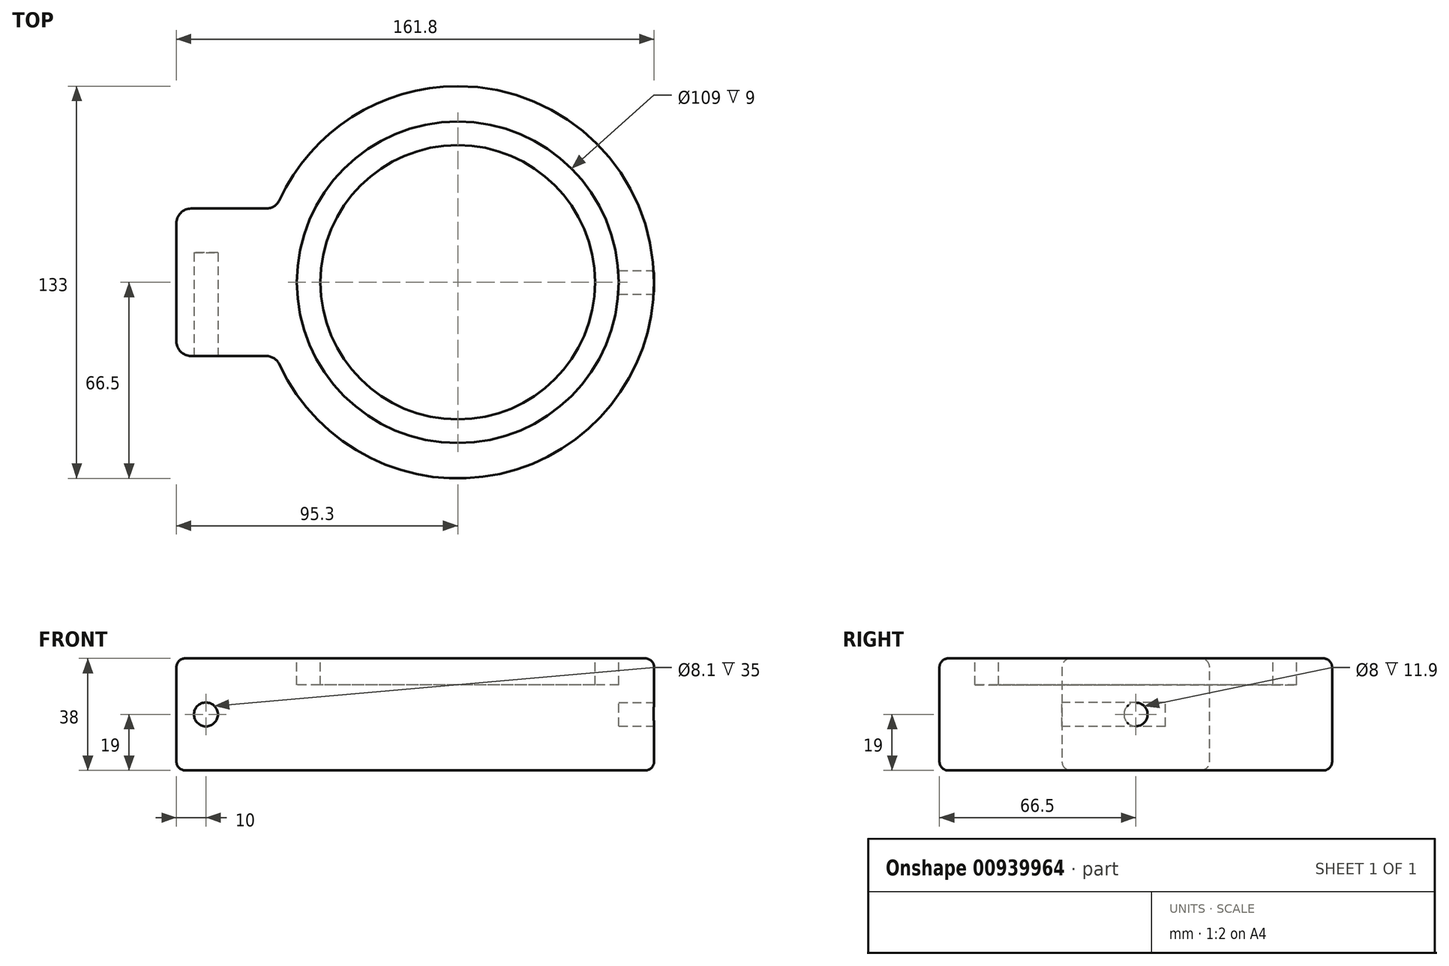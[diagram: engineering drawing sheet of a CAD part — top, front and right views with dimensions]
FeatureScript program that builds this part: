
annotation { "Feature Type Name" : "Feature", "Feature Type Description" : "" }
export const myFeature = defineFeature(function(context is Context, id is Id, definition is map)
    precondition{}
    {
        {
            var Q0;
            Q0=qCreatedBy(makeId("Top.planeOp"),FACE);
            var sketch = newSketch(context, id + "F0", { "sketchPlane" : qUnion([Q0])});
            skArc(sketch, "E0", {"start": v(-61.62, -25) * mm, "mid": v(66.5, 0) * mm, "end": v(-61.62, 25) * mm});
            skLineSegment(sketch, "E1", {"start": v(-61.62, 25) * mm, "end": v(-95.3, 25) * mm});
            skLineSegment(sketch, "E2", {"start": v(-95.3, 25) * mm, "end": v(-95.3, -25) * mm});
            skLineSegment(sketch, "E3", {"start": v(-95.3, -25) * mm, "end": v(-61.62, -25) * mm});
            skPoint(sketch, "E4.orphan", {"position": v(0, -25) * mm});
            skLineSegment(sketch, "E5", {"start": v(0, 66.5) * mm, "end": v(66.5, 66.5) * mm});
            skPoint(sketch, "E5.endSnap0", {"position": v(66.5, 0) * mm});
            skLineSegment(sketch, "E6", {"start": v(66.5, 66.5) * mm, "end": v(66.5, -67.23) * mm});
            skLineSegment(sketch, "E7", {"start": v(66.5, -67.23) * mm, "end": v(0, -66.5) * mm});
            skSolve(sketch);
        }
        {
            var Q0;
            Q0 = qSketchRegion(id + "F0", true);
            extrude(context, id + "F1", {"entities" : qUnion([Q0]), "depth" : 38 * mm, "offsetDistance" : 25 * mm});
        }
        {
            var Q0;
            Q0=makeQuery(id+"F1.opExtrude","SWEPT_EDGE",EDGE,{"disambiguationData":[OSD([sQuery(id+"F0.wireOp",EDGE,"E0"),sQuery(id+"F0.wireOp",EDGE,"E3")])]});
            var Q1;
            Q1=makeQuery(id+"F1.opExtrude","SWEPT_EDGE",EDGE,{"disambiguationData":[OSD([sQuery(id+"F0.wireOp",EDGE,"E0"),sQuery(id+"F0.wireOp",EDGE,"E1")])]});
            var Q2;
            Q2=makeQuery(id+"F1.opExtrude","SWEPT_EDGE",EDGE,{"disambiguationData":[OSD([sQuery(id+"F0.wireOp",EDGE,"E2"),sQuery(id+"F0.wireOp",EDGE,"E3")])]});
            var Q3;
            Q3=makeQuery(id+"F1.opExtrude","SWEPT_EDGE",EDGE,{"disambiguationData":[OSD([sQuery(id+"F0.wireOp",EDGE,"E1"),sQuery(id+"F0.wireOp",EDGE,"E2")])]});
            fillet(context, id + "F2", {"entities" : qUnion([Q0, Q1, Q2, Q3]), "radius" : 5 * mm, "tangentPropagation" : true, "allowEdgeOverflow" : false});
        }
        {
            var Q0;
            Q0=makeQuery(id+"F1.opExtrude","CAP_EDGE",EDGE,{"disambiguationData":[OSD([sQuery(id+"F0.wireOp",EDGE,"E2")])],"isStart":false});
            var Q1;
            Q1=makeQuery(id+"F1.opExtrude","CAP_EDGE",EDGE,{"disambiguationData":[OSD([sQuery(id+"F0.wireOp",EDGE,"E2")])],"isStart":true});
            fillet(context, id + "F3", {"entities" : qUnion([Q0, Q1]), "radius" : 3 * mm, "tangentPropagation" : true, "allowEdgeOverflow" : false});
        }
        {
            var Q0;
            Q0=makeQuery(id+"F1.opExtrude","SWEPT_FACE",FACE,{"disambiguationData":[OSD([sQuery(id+"F0.wireOp",EDGE,"E3")])]});
            var sketch = newSketch(context, id + "F4", { "sketchPlane" : qUnion([Q0])});
            skCircle(sketch, "E8", {"center": v(-85.3, 19) * mm, "radius": 4.05 * mm});
            skSolve(sketch);
        }
        {
            var Q0;
            Q0 = qSketchRegion(id + "F4", true);
            extrude(context, id + "F5", {"entities" : qUnion([Q0]), "operationType" : NewBodyOperationType.REMOVE, "oppositeDirection" : true, "depth" : 35 * mm, "offsetDistance" : 25 * mm});
        }
        {
            var Q0;
            Q0=makeQuery(id+"F1.opExtrude","SWEPT_FACE",FACE,{"disambiguationData":[OSD([sQuery(id+"F0.wireOp",EDGE,"E6")])]});
            var sketch = newSketch(context, id + "F6", { "sketchPlane" : qUnion([Q0])});
            skCircle(sketch, "E9", {"center": v(0, 19) * mm, "radius": 4 * mm});
            skSolve(sketch);
        }
        {
            var Q0;
            Q0 = qSketchRegion(id + "F6", true);
            extrude(context, id + "F7", {"entities" : qUnion([Q0]), "operationType" : NewBodyOperationType.REMOVE, "oppositeDirection" : true, "depth" : 11.9 * mm, "offsetDistance" : 25 * mm});
        }
        {
            var Q0;
            Q0=makeQuery(id+"F1.opExtrude","SWEPT_EDGE",EDGE,{"disambiguationData":[OSD([sQuery(id+"F0.wireOp",EDGE,"E5"),sQuery(id+"F0.wireOp",EDGE,"E6")])]});
            fillet(context, id + "F8", {"entities" : qUnion([Q0]), "radius" : 66.5 * mm, "tangentPropagation" : true, "allowEdgeOverflow" : false});
        }
        {
            var Q0;
            Q0=makeQuery(id+"F1.opExtrude","CAP_FACE",FACE,{"disambiguationData":[OSD([sQuery(id+"F0.wireOp",EDGE,"E0"),sQuery(id+"F0.wireOp",EDGE,"E1"),sQuery(id+"F0.wireOp",EDGE,"E2"),sQuery(id+"F0.wireOp",EDGE,"E3"),sQuery(id+"F0.wireOp",EDGE,"E5"),sQuery(id+"F0.wireOp",EDGE,"E6")])],"isStart":false});
            var sketch = newSketch(context, id + "F9", { "sketchPlane" : qUnion([Q0])});
            skCircle(sketch, "E10", {"center": v(0, 0) * mm, "radius": 46.5 * mm});
            skCircle(sketch, "E11", {"center": v(0, 0) * mm, "radius": 54.5 * mm});
            skSolve(sketch);
        }
        {
            var Q0;
            Q0 = qSketchRegion(id + "F9", true);
            extrude(context, id + "F10", {"entities" : qUnion([Q0]), "operationType" : NewBodyOperationType.REMOVE, "oppositeDirection" : true, "depth" : 9 * mm, "offsetDistance" : 25 * mm});
        }
    });
